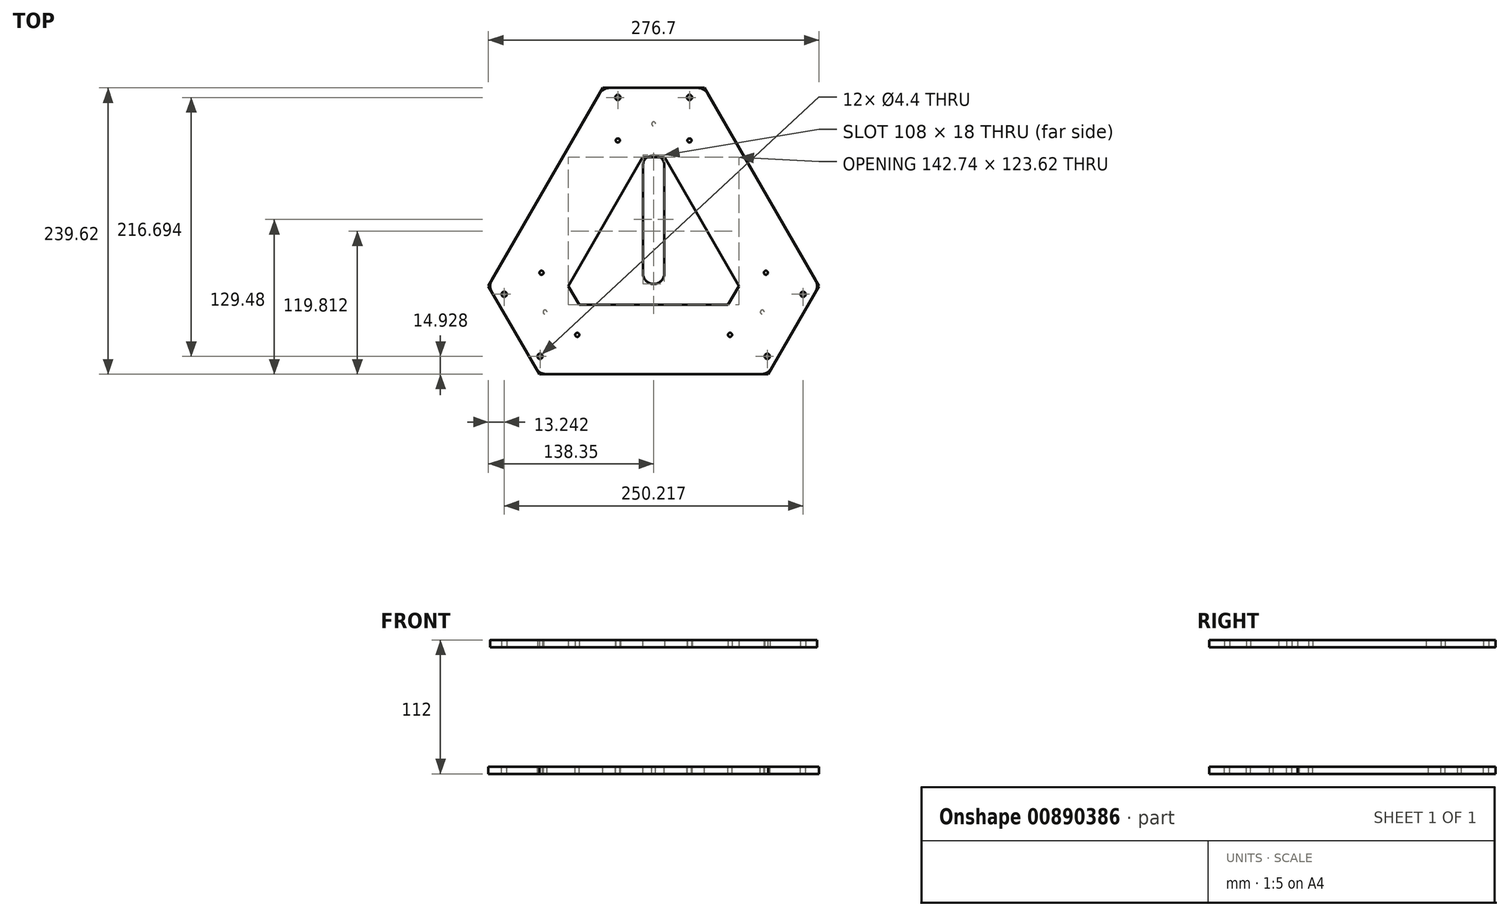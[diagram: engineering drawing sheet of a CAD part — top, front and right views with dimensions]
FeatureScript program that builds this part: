
annotation { "Feature Type Name" : "Feature", "Feature Type Description" : "" }
export const myFeature = defineFeature(function(context is Context, id is Id, definition is map)
    precondition{}
    {
        {
            var Q0;
            Q0=qCreatedBy(makeId("Top.planeOp"),FACE);
            var sketch = newSketch(context, id + "F0", { "sketchPlane" : qUnion([Q0])});
            skLineSegment(sketch, "E0", {"start": v(-138.34, -30.66) * mm, "end": v(-42.62, 135.14) * mm});
            skLineSegment(sketch, "E1", {"start": v(-42.62, 135.14) * mm, "end": v(42.62, 135.14) * mm});
            skLineSegment(sketch, "E2", {"start": v(42.62, 135.14) * mm, "end": v(138.34, -30.66) * mm});
            skLineSegment(sketch, "E3", {"start": v(138.34, -30.66) * mm, "end": v(95.73, -104.48) * mm});
            skLineSegment(sketch, "E4", {"start": v(95.73, -104.48) * mm, "end": v(-95.73, -104.48) * mm});
            skLineSegment(sketch, "E5", {"start": v(-95.73, -104.48) * mm, "end": v(-138.34, -30.66) * mm});
            skLineSegment(sketch, "E6", {"start": v(-90.48, 52.24) * mm, "end": v(0, 0) * mm, "construction": true});
            skLineSegment(sketch, "E7", {"start": v(0, -104.48) * mm, "end": v(0, 0) * mm, "construction": true});
            skLineSegment(sketch, "E8", {"start": v(90.48, 52.24) * mm, "end": v(0, 0) * mm, "construction": true});
            skPoint(sketch, "E9", {"position": v(0, 0) * mm});
            skLineSegment(sketch, "E10.0", {"start": v(62.24, -46.48) * mm, "end": v(-62.24, -46.48) * mm});
            skLineSegment(sketch, "E10.1", {"start": v(-71.37, -30.66) * mm, "end": v(-9.13, 77.14) * mm});
            skLineSegment(sketch, "E10.2", {"start": v(-9.13, 77.14) * mm, "end": v(9.13, 77.14) * mm});
            skLineSegment(sketch, "E10.3", {"start": v(-62.24, -46.48) * mm, "end": v(-71.37, -30.66) * mm});
            skLineSegment(sketch, "E10.4", {"start": v(9.13, 77.14) * mm, "end": v(71.37, -30.66) * mm});
            skLineSegment(sketch, "E10.5", {"start": v(71.37, -30.66) * mm, "end": v(62.24, -46.48) * mm});
            skCircle(sketch, "E11", {"center": v(95.1, -89.55) * mm, "radius": 2.2 * mm});
            skLineSegment(sketch, "E12", {"start": v(117.04, -67.57) * mm, "end": v(66.8, -38.57) * mm, "construction": true});
            skCircle(sketch, "E13", {"center": v(63.93, -71.55) * mm, "radius": 1.7 * mm});
            skCircle(sketch, "E14.MirrorC", {"center": v(93.93, -19.6) * mm, "radius": 1.7 * mm});
            skCircle(sketch, "E15.MirrorC", {"center": v(125.1, -37.6) * mm, "radius": 2.2 * mm});
            skPoint(sketch, "E16.center", {"position": v(-138.5, -32.62) * mm});
            skLineSegment(sketch, "E17.0", {"start": v(95.1, -89.55) * mm, "end": v(95.1, -89.55) * mm});
            skLineSegment(sketch, "E17.1", {"start": v(95.1, -89.55) * mm, "end": v(63.93, -71.55) * mm, "construction": true});
            skCircle(sketch, "E18.1.0", {"center": v(-30, 91.14) * mm, "radius": 1.7 * mm});
            skCircle(sketch, "E18.1.1", {"center": v(-30, 127.14) * mm, "radius": 2.2 * mm});
            skCircle(sketch, "E18.1.2", {"center": v(30, 127.14) * mm, "radius": 2.2 * mm});
            skCircle(sketch, "E18.1.3", {"center": v(30, 91.14) * mm, "radius": 1.7 * mm});
            skCircle(sketch, "E18.2.0", {"center": v(-63.93, -71.55) * mm, "radius": 1.7 * mm});
            skCircle(sketch, "E18.2.1", {"center": v(-95.1, -89.55) * mm, "radius": 2.2 * mm});
            skCircle(sketch, "E18.2.2", {"center": v(-125.1, -37.6) * mm, "radius": 2.2 * mm});
            skCircle(sketch, "E18.2.3", {"center": v(-93.93, -19.6) * mm, "radius": 1.7 * mm});
            skSolve(sketch);
        }
        {
            var Q0;
            {var subQ0=sQuery(id+"F0.wireOp",EDGE,"vAaXFV3b-EpbO-ac0L-dCJ6-TkjUisyF59UN");Q0=makeQuery(id+"F0.imprint","IMPRINT",FACE,{"disambiguationData":[TD([[makeQuery(id+"F0.imprint","IMPRINT",EDGE,{"derivedFrom":subQ0}),1.0]])]});}
            var Q1;
            Q1=makeQuery(id+"F0.imprint","IMPRINT",FACE,{"disambiguationData":[TD([[makeQuery(id+"F0.imprint","IMPRINT",EDGE,{"derivedFrom":sQuery(id+"F0.wireOp",EDGE,"E0")}),-1.0]])]});
            extrude(context, id + "F1", {"entities" : qUnion([Q0, Q1]), "depth" : 6 * mm, "offsetDistance" : 25 * mm});
        }
        {
            var Q0;
            Q0=makeQuery(id+"F1.opExtrude","CAP_FACE",FACE,{"disambiguationData":[OSD([sQuery(id+"F0.wireOp",EDGE,"E0"),sQuery(id+"F0.wireOp",EDGE,"E1"),sQuery(id+"F0.wireOp",EDGE,"E2"),sQuery(id+"F0.wireOp",EDGE,"E3"),sQuery(id+"F0.wireOp",EDGE,"E4"),sQuery(id+"F0.wireOp",EDGE,"E5"),sQuery(id+"F0.wireOp",EDGE,"E10.0"),sQuery(id+"F0.wireOp",EDGE,"E10.1"),sQuery(id+"F0.wireOp",EDGE,"E10.2"),sQuery(id+"F0.wireOp",EDGE,"E10.3"),sQuery(id+"F0.wireOp",EDGE,"E10.4"),sQuery(id+"F0.wireOp",EDGE,"E10.5")])],"isStart":true});
            cPlane(context, id + "F2", {"entities" : qUnion([Q0]), "cplaneType" : CPlaneType.OFFSET, "offset" : 100 * mm, "width" : 150 * mm, "height" : 150 * mm});
        }
        {
            var Q0;
            Q0=qCreatedBy(id+"F2.planeOp",FACE);
            var sketch = newSketch(context, id + "F3", { "sketchPlane" : qUnion([Q0])});
            skLineSegment(sketch, "E19", {"start": v(-95.73, 104.48) * mm, "end": v(95.73, 104.48) * mm});
            skLineSegment(sketch, "E20", {"start": v(95.73, 104.48) * mm, "end": v(138.34, 30.66) * mm});
            skLineSegment(sketch, "E21", {"start": v(138.34, 30.66) * mm, "end": v(42.62, -135.14) * mm});
            skLineSegment(sketch, "E22", {"start": v(42.62, -135.14) * mm, "end": v(-42.62, -135.14) * mm});
            skLineSegment(sketch, "E23", {"start": v(-42.62, -135.14) * mm, "end": v(-138.34, 30.66) * mm});
            skLineSegment(sketch, "E24", {"start": v(-138.34, 30.66) * mm, "end": v(-95.73, 104.48) * mm});
            skLineSegment(sketch, "E25", {"start": v(-90.48, -52.24) * mm, "end": v(0, 0) * mm, "construction": true});
            skLineSegment(sketch, "E26", {"start": v(90.48, -52.24) * mm, "end": v(0, 0) * mm, "construction": true});
            skLineSegment(sketch, "E27", {"start": v(0, 104.48) * mm, "end": v(0, 0) * mm, "construction": true});
            skCircle(sketch, "E28", {"center": v(-30, -127.14) * mm, "radius": 2.2 * mm});
            skCircle(sketch, "E29", {"center": v(30, -127.14) * mm, "radius": 2.2 * mm});
            skCircle(sketch, "E30", {"center": v(-30, -91.14) * mm, "radius": 1.7 * mm});
            skCircle(sketch, "E31", {"center": v(30, -91.14) * mm, "radius": 1.7 * mm});
            skCircle(sketch, "E32", {"center": v(0, 0) * mm, "radius": 110 * mm, "construction": true});
            skCircle(sketch, "E33", {"center": v(0, -105) * mm, "radius": 1.65 * mm});
            skCircle(sketch, "E34.1.0", {"center": v(90.93, 52.5) * mm, "radius": 1.65 * mm});
            skCircle(sketch, "E34.2.0", {"center": v(-90.93, 52.5) * mm, "radius": 1.65 * mm});
            skCircle(sketch, "E35.1.0", {"center": v(125.1, 37.6) * mm, "radius": 2.2 * mm});
            skCircle(sketch, "E35.1.1", {"center": v(95.1, 89.55) * mm, "radius": 2.2 * mm});
            skCircle(sketch, "E35.1.2", {"center": v(63.93, 71.55) * mm, "radius": 1.7 * mm});
            skCircle(sketch, "E35.1.3", {"center": v(93.93, 19.6) * mm, "radius": 1.7 * mm});
            skCircle(sketch, "E35.2.0", {"center": v(-95.1, 89.55) * mm, "radius": 2.2 * mm});
            skCircle(sketch, "E35.2.1", {"center": v(-125.1, 37.6) * mm, "radius": 2.2 * mm});
            skCircle(sketch, "E35.2.2", {"center": v(-93.93, 19.6) * mm, "radius": 1.7 * mm});
            skCircle(sketch, "E35.2.3", {"center": v(-63.93, 71.55) * mm, "radius": 1.7 * mm});
            skLineSegment(sketch, "E36", {"start": v(0, 20) * mm, "end": v(0, -70) * mm, "construction": true});
            skArc(sketch, "E37.0.startCap", {"start": v(-9, 20) * mm, "mid": v(0, 29) * mm, "end": v(9, 20) * mm});
            skArc(sketch, "E37.0.endCap", {"start": v(9, -70) * mm, "mid": v(0, -79) * mm, "end": v(-9, -70) * mm});
            skLineSegment(sketch, "E37.0.left", {"start": v(9, 20) * mm, "end": v(9, -70) * mm});
            skLineSegment(sketch, "E37.0.right", {"start": v(-9, 20) * mm, "end": v(-9, -70) * mm});
            skSolve(sketch);
        }
        {
            var Q0;
            Q0=qSketchRegion(id+"F3",true);
            extrude(context, id + "F4", {"entities" : qUnion([Q0]), "depth" : 6 * mm, "offsetDistance" : 25 * mm});
        }
        {
            var Q0;
            Q0=makeQuery(id+"F1.opExtrude","SWEPT_EDGE",EDGE,{"disambiguationData":[OSD([sQuery(id+"F0.wireOp",EDGE,"E3"),sQuery(id+"F0.wireOp",EDGE,"E4")])]});
            var Q1;
            Q1=makeQuery(id+"F1.opExtrude","SWEPT_EDGE",EDGE,{"disambiguationData":[OSD([sQuery(id+"F0.wireOp",EDGE,"E2"),sQuery(id+"F0.wireOp",EDGE,"E3")])]});
            var Q2;
            Q2=makeQuery(id+"F1.opExtrude","SWEPT_EDGE",EDGE,{"disambiguationData":[OSD([sQuery(id+"F0.wireOp",EDGE,"E4"),sQuery(id+"F0.wireOp",EDGE,"E5")])]});
            var Q3;
            Q3=makeQuery(id+"F1.opExtrude","SWEPT_EDGE",EDGE,{"disambiguationData":[OSD([sQuery(id+"F0.wireOp",EDGE,"E0"),sQuery(id+"F0.wireOp",EDGE,"E5")])]});
            var Q4;
            Q4=makeQuery(id+"F1.opExtrude","SWEPT_EDGE",EDGE,{"disambiguationData":[OSD([sQuery(id+"F0.wireOp",EDGE,"E0"),sQuery(id+"F0.wireOp",EDGE,"E1")])]});
            var Q5;
            Q5=makeQuery(id+"F1.opExtrude","SWEPT_EDGE",EDGE,{"disambiguationData":[OSD([sQuery(id+"F0.wireOp",EDGE,"E1"),sQuery(id+"F0.wireOp",EDGE,"E2")])]});
            var Q6;
            Q6=makeQuery(id+"F4.opExtrude","SWEPT_EDGE",EDGE,{"disambiguationData":[OSD([sQuery(id+"F3.wireOp",EDGE,"6d3ae851-c3e5-4c5a-856b-07c4a10c4b37"),sQuery(id+"F3.wireOp",EDGE,"cf7309b4-70c5-4301-b6ed-71b964c1edfa")])]});
            var Q7;
            Q7=makeQuery(id+"F4.opExtrude","SWEPT_EDGE",EDGE,{"disambiguationData":[OSD([sQuery(id+"F3.wireOp",EDGE,"3a46702a-baa6-40e6-a59b-8ada2e90e725"),sQuery(id+"F3.wireOp",EDGE,"6d3ae851-c3e5-4c5a-856b-07c4a10c4b37")])]});
            var Q8;
            Q8=makeQuery(id+"F4.opExtrude","SWEPT_EDGE",EDGE,{"disambiguationData":[OSD([sQuery(id+"F3.wireOp",EDGE,"3a46702a-baa6-40e6-a59b-8ada2e90e725"),sQuery(id+"F3.wireOp",EDGE,"78cf180f-0592-4679-8161-a94ec011c997")])]});
            var Q9;
            Q9=makeQuery(id+"F4.opExtrude","SWEPT_EDGE",EDGE,{"disambiguationData":[OSD([sQuery(id+"F3.wireOp",EDGE,"b5e919fd-7c42-47fd-8e9d-da210d86f053"),sQuery(id+"F3.wireOp",EDGE,"78cf180f-0592-4679-8161-a94ec011c997")])]});
            var Q10;
            Q10=makeQuery(id+"F4.opExtrude","SWEPT_EDGE",EDGE,{"disambiguationData":[OSD([sQuery(id+"F3.wireOp",EDGE,"32e224b0-ec15-409d-8985-8497f9395f18"),sQuery(id+"F3.wireOp",EDGE,"b5e919fd-7c42-47fd-8e9d-da210d86f053")])]});
            var Q11;
            Q11=makeQuery(id+"F4.opExtrude","SWEPT_EDGE",EDGE,{"disambiguationData":[OSD([sQuery(id+"F3.wireOp",EDGE,"cf7309b4-70c5-4301-b6ed-71b964c1edfa"),sQuery(id+"F3.wireOp",EDGE,"32e224b0-ec15-409d-8985-8497f9395f18")])]});
            fillet(context, id + "F5", {"entities" : qUnion([Q0, Q1, Q2, Q3, Q4, Q5, Q6, Q7, Q8, Q9, Q10, Q11]), "radius" : 10 * mm, "tangentPropagation" : true, "allowEdgeOverflow" : false});
        }
    });
